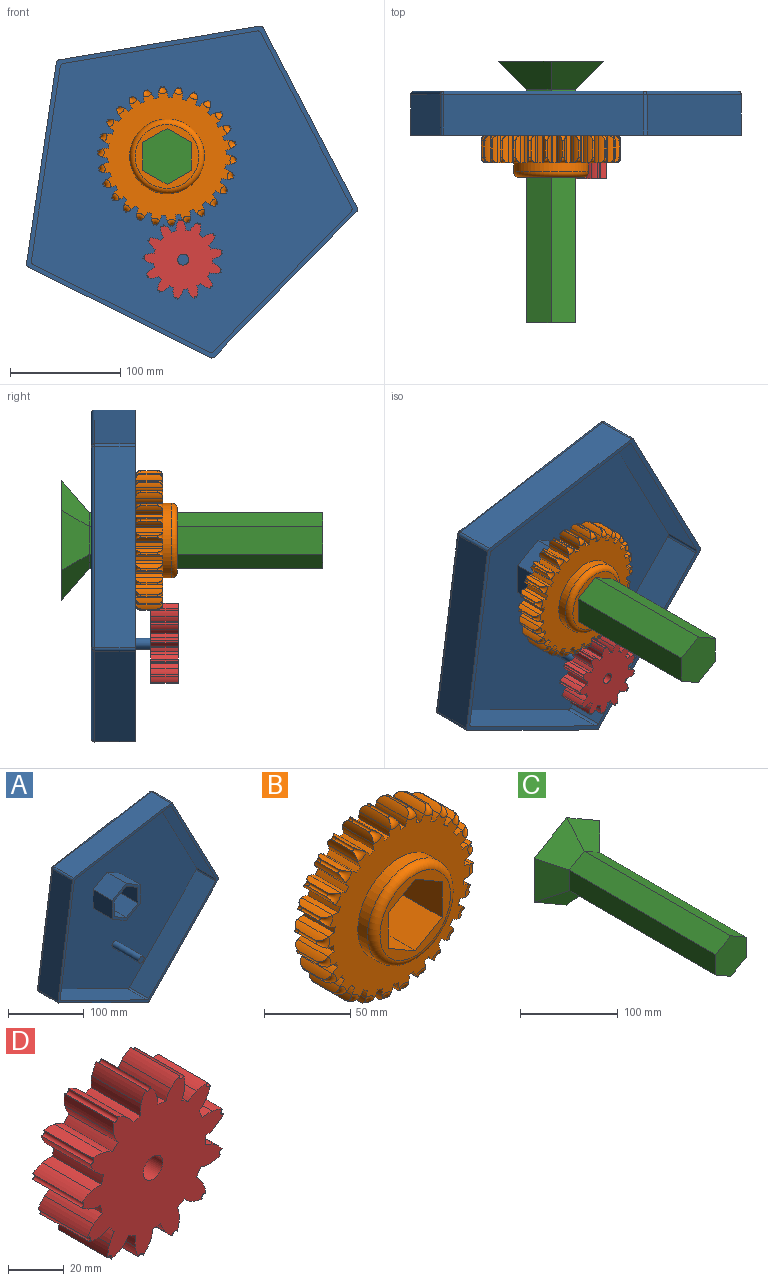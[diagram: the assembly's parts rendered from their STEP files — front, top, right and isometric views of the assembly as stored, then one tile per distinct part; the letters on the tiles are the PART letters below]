
ASSEMBLY  parts=4 mates=3
PART A: 48 faces, bbox 300.4x54x301.4 mm
  f0: plane 301.37x300.44mm, normal (0,-1,0), area 3719.9mm2, adj f6,f7,f8,f9,f10,f19,f20,f21
  f1: plane 40x22mm, normal (-0.5,0,-0.87), area 1016mm2, adj f2,f11,f12,f13
  f2: plane 40x25.4mm, normal (-1,0,0), area 1016mm2, adj f1,f3,f12,f13
  f3: plane 40x22mm, normal (-0.5,0,0.87), area 1016mm2, adj f2,f4,f12,f13
  f4: plane 40x22mm, normal (0.5,0,0.87), area 1016mm2, adj f3,f5,f12,f13
  f5: plane 40x25.4mm, normal (1,0,0), area 1016mm2, adj f4,f11,f12,f13
  f6: plane 131.78x129.19mm, normal (0.71,0,-0.7), area 6828mm2, adj f0,f39,f43,f45
  f7: plane 163.59x85.41mm, normal (0.89,0,0.46), area 6828mm2, adj f0,f36,f42,f45
  f8: plane 181.97x37mm, normal (-0.17,0,0.99), area 6828mm2, adj f0,f31,f36,f37
  f9: plane 182.55x37mm, normal (-0.99,0,0.15), area 6828mm2, adj f0,f31,f32,f33
  f10: plane 165.25x82.14mm, normal (-0.45,0,-0.9), area 6828mm2, adj f0,f33,f38,f39
  f11: plane 40x22mm, normal (0.5,0,-0.87), area 1016mm2, adj f1,f5,f12,f13
  f12: plane 60.04x51.99mm, normal (0,-1,0), area 665mm2, adj f1,f2,f3,f4,f5,f11,f14,f15
  f13: plane 295.37x294.44mm, normal (0,1,0), area 56915.8mm2, adj f1,f2,f3,f4,f5,f11,f32,f37
  f14: plane 36x26mm, normal (0.5,0,0.87), area 1080.7mm2, adj f12,f15,f24,f25
  f15: plane 36x30.02mm, normal (1,0,0), area 1080.7mm2, adj f12,f14,f16,f25
  f16: plane 36x26mm, normal (0.5,0,-0.87), area 1080.7mm2, adj f12,f15,f17,f25
  f17: plane 36x26mm, normal (-0.5,0,-0.87), area 1080.7mm2, adj f12,f16,f18,f25
  f18: plane 36x30.02mm, normal (-1,0,0), area 1080.7mm2, adj f12,f17,f24,f25
  f19: plane 127.63x125.12mm, normal (-0.71,0,0.7), area 6434.3mm2, adj f0,f25,f26,f30
  f20: plane 158.43x82.72mm, normal (-0.89,0,-0.46), area 6434.3mm2, adj f0,f25,f26,f27
  f21: plane 176.24x36mm, normal (0.17,0,-0.99), area 6434.3mm2, adj f0,f25,f27,f28
  f22: plane 176.8x36mm, normal (0.99,0,-0.15), area 6434.3mm2, adj f0,f25,f28,f29
  f23: plane 160.05x79.55mm, normal (0.45,0,0.9), area 6434.3mm2, adj f0,f25,f29,f30
  f24: plane 36x26mm, normal (-0.5,0,0.87), area 1080.7mm2, adj f12,f14,f18,f25
  f25: plane 292.07x291.17mm, normal (0,-1,0), area 55248.8mm2, adj f14,f15,f16,f17,f18,f19,f20,f21
  f26: cylinder r=3mm len=36mm, axis (0,-1,0), area 135.7mm2, adj f0,f19,f20,f25
  f27: cylinder r=3mm len=36mm, axis (0,-1,0), area 135.7mm2, adj f0,f20,f21,f25
  f28: cylinder r=3mm len=36mm, axis (0,-1,0), area 135.7mm2, adj f0,f21,f22,f25
  f29: cylinder r=3mm len=36mm, axis (0,-1,0), area 135.7mm2, adj f0,f22,f23,f25
  f30: cylinder r=3mm len=36mm, axis (0,-1,0), area 135.7mm2, adj f0,f19,f23,f25
  f31: cylinder r=3mm len=37mm, axis (0,1,0), area 139.5mm2, adj f0,f8,f9,f34
  f32: cylinder r=3mm len=182.99mm, axis (-0.15,0,-0.99), area 869.6mm2, adj f9,f13,f34,f35
  f33: cylinder r=3mm len=37mm, axis (0,1,0), area 139.5mm2, adj f0,f9,f10,f35
  f34: sphere r=3mm, area 11.3mm2, adj f31,f32,f37
  f35: sphere r=3mm, area 11.3mm2, adj f32,f33,f38
  f36: cylinder r=3mm len=37mm, axis (0,1,0), area 139.5mm2, adj f0,f7,f8,f40
  f37: cylinder r=3mm len=182.47mm, axis (-0.99,0,-0.17), area 869.6mm2, adj f8,f13,f34,f40
  f38: cylinder r=3mm len=166.59mm, axis (0.9,0,-0.45), area 869.6mm2, adj f10,f13,f35,f41
  f39: cylinder r=3mm len=37mm, axis (0,1,0), area 139.5mm2, adj f0,f6,f10,f41
  f40: sphere r=3mm, area 11.3mm2, adj f36,f37,f42
  f41: sphere r=3mm, area 11.3mm2, adj f38,f39,f43
  f42: cylinder r=3mm len=164.97mm, axis (-0.46,0,0.89), area 869.6mm2, adj f7,f13,f40,f44
  f43: cylinder r=3mm len=133.88mm, axis (0.7,0,0.71), area 869.6mm2, adj f6,f13,f41,f44
  f44: sphere r=3mm, area 11.3mm2, adj f42,f43,f45
  f45: cylinder r=3mm len=37mm, axis (0,1,0), area 139.5mm2, adj f0,f6,f7,f44
  f46: cylinder r=5mm len=50mm, axis (0,1,0), area 1570.8mm2, adj f25,f47
  f47: plane 10x10mm, normal (0,-1,0), area 78.5mm2, adj f46
PART B: 218 faces, bbox 128.7x38.1x128.8 mm
  f0: cylinder r=53.72mm len=25mm, axis (0,1,0), area 100.1mm2, adj f30,f31,f32,f133
  f1: cylinder r=53.72mm len=25mm, axis (0,1,0), area 100.1mm2, adj f31,f32,f126,f132
  f2: cylinder r=53.72mm len=25mm, axis (0,1,0), area 100.1mm2, adj f31,f32,f119,f125
  f3: cylinder r=53.72mm len=25mm, axis (0,1,0), area 100.1mm2, adj f31,f32,f112,f118
  f4: cylinder r=53.72mm len=25mm, axis (0,1,0), area 100.1mm2, adj f31,f32,f105,f111
  f5: cylinder r=53.72mm len=25mm, axis (0,1,0), area 100.1mm2, adj f31,f32,f98,f104
  f6: cylinder r=53.72mm len=25mm, axis (0,1,0), area 100.1mm2, adj f31,f32,f91,f97
  f7: cylinder r=53.72mm len=25mm, axis (0,1,0), area 100.1mm2, adj f31,f32,f84,f90
  f8: cylinder r=53.72mm len=25mm, axis (0,1,0), area 100.1mm2, adj f31,f32,f77,f83
  f9: cylinder r=53.72mm len=25mm, axis (0,1,0), area 100.1mm2, adj f31,f32,f70,f76
  f10: cylinder r=53.72mm len=25mm, axis (0,1,0), area 100.1mm2, adj f31,f32,f63,f69
  f11: cylinder r=53.72mm len=25mm, axis (0,1,0), area 100.1mm2, adj f31,f32,f56,f62
  f12: cylinder r=53.72mm len=25mm, axis (0,1,0), area 100.1mm2, adj f31,f32,f49,f55
  f13: cylinder r=53.72mm len=25mm, axis (0,1,0), area 100.1mm2, adj f31,f32,f48,f210
  f14: cylinder r=53.72mm len=25mm, axis (0,1,0), area 100.1mm2, adj f31,f32,f209,f214
  f15: cylinder r=53.72mm len=25mm, axis (0,1,0), area 100.1mm2, adj f31,f32,f202,f208
  f16: cylinder r=53.72mm len=25mm, axis (0,1,0), area 100.1mm2, adj f31,f32,f195,f201
  f17: cylinder r=53.72mm len=25mm, axis (0,1,0), area 100.1mm2, adj f31,f32,f188,f194
  f18: cylinder r=53.72mm len=25mm, axis (0,1,0), area 100.1mm2, adj f31,f32,f182,f187
  f19: cylinder r=53.72mm len=25mm, axis (0,1,0), area 100.1mm2, adj f31,f32,f175,f181
  f20: cylinder r=53.72mm len=25mm, axis (0,1,0), area 100.1mm2, adj f31,f32,f168,f174
  f21: cylinder r=53.72mm len=25mm, axis (0,1,0), area 100.1mm2, adj f31,f32,f161,f167
  f22: cylinder r=53.72mm len=25mm, axis (0,1,0), area 100.1mm2, adj f31,f32,f154,f160
  f23: cylinder r=53.72mm len=25mm, axis (0,1,0), area 100.1mm2, adj f31,f32,f147,f153
  f24: cylinder r=53.72mm len=25mm, axis (0,1,0), area 100.1mm2, adj f31,f32,f139,f146
  f25: cylinder r=53.72mm len=25mm, axis (0,1,0), area 100.1mm2, adj f26,f31,f32,f140
  f26: cylinder r=14.2mm len=25mm, axis (0,1,0), area 127.1mm2, adj f25,f27,f31,f32
  f27: cylinder r=14.99mm len=25mm, axis (0,1,0), area 128mm2, adj f26,f28,f31,f32,f33,f34
  f28: cylinder r=1.17mm len=14.84mm, axis (0,1,0), area 54.3mm2, adj f27,f29,f33,f34
  f29: cylinder r=14.99mm len=25mm, axis (0,1,0), area 128mm2, adj f28,f30,f31,f32,f33,f34
  f30: cylinder r=14.2mm len=25mm, axis (0,1,0), area 127.1mm2, adj f0,f29,f31,f32
  f31: plane 117.37x117.36mm, normal (0,-1,0), area 6357.2mm2, adj f0,f1,f2,f3,f4,f5,f6,f7
  f32: plane 119.73x117.37mm, normal (0,1,0), area 8340.6mm2, adj f0,f1,f2,f3,f4,f5,f6,f7
  f33: torus R=6.25mm, axis (0,-1,0), area 43.9mm2, adj f27,f28,f29,f32
  f34: torus R=6.25mm, axis (0,-1,0), area 43.9mm2, adj f27,f28,f29,f31
  f35: plane 38.1x25.4mm, normal (-1,0,0), area 967.7mm2, adj f32,f36,f40,f42
  f36: plane 38.1x22mm, normal (-0.5,0,0.87), area 967.7mm2, adj f32,f35,f37,f40
  f37: plane 38.1x22mm, normal (0.5,0,0.87), area 967.7mm2, adj f32,f36,f38,f40
  f38: plane 38.1x25.4mm, normal (1,0,0), area 967.7mm2, adj f32,f37,f39,f40
  f39: plane 38.1x22mm, normal (0.5,0,-0.87), area 967.7mm2, adj f32,f38,f40,f42
  f40: plane 57.81x57.81mm, normal (0,-1,0), area 948.4mm2, adj f35,f36,f37,f38,f39,f42,f217
  f41: cylinder r=33.98mm len=67.97mm, axis (0,1,0), area 1712.5mm2, adj f31,f217
  f42: plane 38.1x22mm, normal (-0.5,0,-0.87), area 967.7mm2, adj f32,f35,f39,f40
  f43: cylinder r=1.17mm len=14.84mm, axis (0,1,0), area 54.3mm2, adj f44,f45,f46,f47
  f44: torus R=6.25mm, axis (0,-1,0), area 43.9mm2, adj f31,f43,f45,f47
  f45: cylinder r=14.99mm len=25mm, axis (0,1,0), area 128mm2, adj f31,f32,f43,f44,f46,f49
  f46: torus R=6.25mm, axis (0,-1,0), area 43.9mm2, adj f32,f43,f45,f47
  f47: cylinder r=14.99mm len=25mm, axis (0,1,0), area 128mm2, adj f31,f32,f43,f44,f46,f48
  f48: cylinder r=14.2mm len=25mm, axis (0,1,0), area 127.1mm2, adj f13,f31,f32,f47
  f49: cylinder r=14.2mm len=25mm, axis (0,1,0), area 127.1mm2, adj f12,f31,f32,f45
  f50: cylinder r=1.17mm len=14.84mm, axis (0,1,0), area 54.3mm2, adj f51,f52,f53,f54
  f51: torus R=6.25mm, axis (0,-1,0), area 43.9mm2, adj f31,f50,f52,f54
  f52: cylinder r=14.99mm len=25mm, axis (0,1,0), area 128mm2, adj f31,f32,f50,f51,f53,f56
  f53: torus R=6.25mm, axis (0,-1,0), area 43.9mm2, adj f32,f50,f52,f54
  f54: cylinder r=14.99mm len=25mm, axis (0,1,0), area 128mm2, adj f31,f32,f50,f51,f53,f55
  f55: cylinder r=14.2mm len=25mm, axis (0,1,0), area 127.1mm2, adj f12,f31,f32,f54
  f56: cylinder r=14.2mm len=25mm, axis (0,1,0), area 127.1mm2, adj f11,f31,f32,f52
  f57: cylinder r=1.17mm len=14.84mm, axis (0,1,0), area 54.3mm2, adj f58,f59,f60,f61
  f58: torus R=6.25mm, axis (0,-1,0), area 43.9mm2, adj f31,f57,f59,f61
  f59: cylinder r=14.99mm len=25mm, axis (0,1,0), area 128mm2, adj f31,f32,f57,f58,f60,f63
  f60: torus R=6.25mm, axis (0,-1,0), area 43.9mm2, adj f32,f57,f59,f61
  f61: cylinder r=14.99mm len=25mm, axis (0,1,0), area 128mm2, adj f31,f32,f57,f58,f60,f62
  f62: cylinder r=14.2mm len=25mm, axis (0,1,0), area 127.1mm2, adj f11,f31,f32,f61
  f63: cylinder r=14.2mm len=25mm, axis (0,1,0), area 127.1mm2, adj f10,f31,f32,f59
  f64: cylinder r=1.17mm len=14.84mm, axis (0,1,0), area 54.3mm2, adj f65,f66,f67,f68
  f65: torus R=6.25mm, axis (0,-1,0), area 43.9mm2, adj f31,f64,f66,f68
  f66: cylinder r=14.99mm len=25mm, axis (0,1,0), area 128mm2, adj f31,f32,f64,f65,f67,f70
  f67: torus R=6.25mm, axis (0,-1,0), area 43.9mm2, adj f32,f64,f66,f68
  f68: cylinder r=14.99mm len=25mm, axis (0,1,0), area 128mm2, adj f31,f32,f64,f65,f67,f69
  f69: cylinder r=14.2mm len=25mm, axis (0,1,0), area 127.1mm2, adj f10,f31,f32,f68
  f70: cylinder r=14.2mm len=25mm, axis (0,1,0), area 127.1mm2, adj f9,f31,f32,f66
  f71: cylinder r=1.17mm len=14.84mm, axis (0,1,0), area 54.3mm2, adj f72,f73,f74,f75
  f72: torus R=6.25mm, axis (0,-1,0), area 43.9mm2, adj f31,f71,f73,f75
  f73: cylinder r=14.99mm len=25mm, axis (0,1,0), area 128mm2, adj f31,f32,f71,f72,f74,f77
  f74: torus R=6.25mm, axis (0,-1,0), area 43.9mm2, adj f32,f71,f73,f75
  f75: cylinder r=14.99mm len=25mm, axis (0,1,0), area 128mm2, adj f31,f32,f71,f72,f74,f76
  f76: cylinder r=14.2mm len=25mm, axis (0,1,0), area 127.1mm2, adj f9,f31,f32,f75
  f77: cylinder r=14.2mm len=25mm, axis (0,1,0), area 127.1mm2, adj f8,f31,f32,f73
  f78: cylinder r=1.17mm len=14.84mm, axis (0,1,0), area 54.3mm2, adj f79,f80,f81,f82
  f79: torus R=6.25mm, axis (0,-1,0), area 43.9mm2, adj f31,f78,f80,f82
  f80: cylinder r=14.99mm len=25mm, axis (0,1,0), area 128mm2, adj f31,f32,f78,f79,f81,f84
  f81: torus R=6.25mm, axis (0,-1,0), area 43.9mm2, adj f32,f78,f80,f82
  f82: cylinder r=14.99mm len=25mm, axis (0,1,0), area 128mm2, adj f31,f32,f78,f79,f81,f83
  f83: cylinder r=14.2mm len=25mm, axis (0,1,0), area 127.1mm2, adj f8,f31,f32,f82
  f84: cylinder r=14.2mm len=25mm, axis (0,1,0), area 127.1mm2, adj f7,f31,f32,f80
  f85: cylinder r=1.17mm len=14.84mm, axis (0,1,0), area 54.3mm2, adj f86,f87,f88,f89
  f86: torus R=6.25mm, axis (0,-1,0), area 43.9mm2, adj f31,f85,f87,f89
  f87: cylinder r=14.99mm len=25mm, axis (0,1,0), area 128mm2, adj f31,f32,f85,f86,f88,f91
  f88: torus R=6.25mm, axis (0,-1,0), area 43.9mm2, adj f32,f85,f87,f89
  f89: cylinder r=14.99mm len=25mm, axis (0,1,0), area 128mm2, adj f31,f32,f85,f86,f88,f90
  f90: cylinder r=14.2mm len=25mm, axis (0,1,0), area 127.1mm2, adj f7,f31,f32,f89
  f91: cylinder r=14.2mm len=25mm, axis (0,1,0), area 127.1mm2, adj f6,f31,f32,f87
  f92: cylinder r=1.17mm len=14.84mm, axis (0,1,0), area 54.3mm2, adj f93,f94,f95,f96
  f93: torus R=6.25mm, axis (0,-1,0), area 43.9mm2, adj f31,f92,f94,f96
  f94: cylinder r=14.99mm len=25mm, axis (0,1,0), area 128mm2, adj f31,f32,f92,f93,f95,f98
  f95: torus R=6.25mm, axis (0,-1,0), area 43.9mm2, adj f32,f92,f94,f96
  f96: cylinder r=14.99mm len=25mm, axis (0,1,0), area 128mm2, adj f31,f32,f92,f93,f95,f97
  f97: cylinder r=14.2mm len=25mm, axis (0,1,0), area 127.1mm2, adj f6,f31,f32,f96
  f98: cylinder r=14.2mm len=25mm, axis (0,1,0), area 127.1mm2, adj f5,f31,f32,f94
  f99: cylinder r=1.17mm len=14.84mm, axis (0,1,0), area 54.3mm2, adj f100,f101,f102,f103
  f100: torus R=6.25mm, axis (0,-1,0), area 43.9mm2, adj f31,f99,f101,f103
  f101: cylinder r=14.99mm len=25mm, axis (0,1,0), area 128mm2, adj f31,f32,f99,f100,f102,f105
  f102: torus R=6.25mm, axis (0,-1,0), area 43.9mm2, adj f32,f99,f101,f103
  f103: cylinder r=14.99mm len=25mm, axis (0,1,0), area 128mm2, adj f31,f32,f99,f100,f102,f104
  f104: cylinder r=14.2mm len=25mm, axis (0,1,0), area 127.1mm2, adj f5,f31,f32,f103
  f105: cylinder r=14.2mm len=25mm, axis (0,1,0), area 127.1mm2, adj f4,f31,f32,f101
  f106: cylinder r=1.17mm len=14.84mm, axis (0,1,0), area 54.3mm2, adj f107,f108,f109,f110
  f107: torus R=6.25mm, axis (0,-1,0), area 43.9mm2, adj f31,f106,f108,f110
  f108: cylinder r=14.99mm len=25mm, axis (0,1,0), area 128mm2, adj f31,f32,f106,f107,f109,f112
  f109: torus R=6.25mm, axis (0,-1,0), area 43.9mm2, adj f32,f106,f108,f110
  f110: cylinder r=14.99mm len=25mm, axis (0,1,0), area 128mm2, adj f31,f32,f106,f107,f109,f111
  f111: cylinder r=14.2mm len=25mm, axis (0,1,0), area 127.1mm2, adj f4,f31,f32,f110
  f112: cylinder r=14.2mm len=25mm, axis (0,1,0), area 127.1mm2, adj f3,f31,f32,f108
  f113: cylinder r=1.17mm len=14.84mm, axis (0,1,0), area 54.3mm2, adj f114,f115,f116,f117
  f114: torus R=6.25mm, axis (0,-1,0), area 43.9mm2, adj f31,f113,f115,f117
  f115: cylinder r=14.99mm len=25mm, axis (0,1,0), area 128mm2, adj f31,f32,f113,f114,f116,f119
  f116: torus R=6.25mm, axis (0,-1,0), area 43.9mm2, adj f32,f113,f115,f117
  f117: cylinder r=14.99mm len=25mm, axis (0,1,0), area 128mm2, adj f31,f32,f113,f114,f116,f118
  f118: cylinder r=14.2mm len=25mm, axis (0,1,0), area 127.1mm2, adj f3,f31,f32,f117
  f119: cylinder r=14.2mm len=25mm, axis (0,1,0), area 127.1mm2, adj f2,f31,f32,f115
  f120: cylinder r=1.17mm len=14.84mm, axis (0,1,0), area 54.3mm2, adj f121,f122,f123,f124
  f121: torus R=6.25mm, axis (0,-1,0), area 43.9mm2, adj f31,f120,f122,f124
  f122: cylinder r=14.99mm len=25mm, axis (0,1,0), area 128mm2, adj f31,f32,f120,f121,f123,f126
  f123: torus R=6.25mm, axis (0,-1,0), area 43.9mm2, adj f32,f120,f122,f124
  f124: cylinder r=14.99mm len=25mm, axis (0,1,0), area 128mm2, adj f31,f32,f120,f121,f123,f125
  f125: cylinder r=14.2mm len=25mm, axis (0,1,0), area 127.1mm2, adj f2,f31,f32,f124
  f126: cylinder r=14.2mm len=25mm, axis (0,1,0), area 127.1mm2, adj f1,f31,f32,f122
  f127: cylinder r=1.17mm len=14.84mm, axis (0,1,0), area 54.3mm2, adj f128,f129,f130,f131
  f128: torus R=6.25mm, axis (0,-1,0), area 43.9mm2, adj f31,f127,f129,f131
  f129: cylinder r=14.99mm len=25mm, axis (0,1,0), area 128mm2, adj f31,f32,f127,f128,f130,f133
  f130: torus R=6.25mm, axis (0,-1,0), area 43.9mm2, adj f32,f127,f129,f131
  f131: cylinder r=14.99mm len=25mm, axis (0,1,0), area 128mm2, adj f31,f32,f127,f128,f130,f132
  f132: cylinder r=14.2mm len=25mm, axis (0,1,0), area 127.1mm2, adj f1,f31,f32,f131
  f133: cylinder r=14.2mm len=25mm, axis (0,1,0), area 127.1mm2, adj f0,f31,f32,f129
  f134: cylinder r=1.17mm len=14.84mm, axis (0,1,0), area 54.3mm2, adj f135,f136,f137,f138
  f135: torus R=6.25mm, axis (0,-1,0), area 43.9mm2, adj f31,f134,f136,f138
  f136: cylinder r=14.99mm len=25mm, axis (0,1,0), area 128mm2, adj f31,f32,f134,f135,f137,f139
  f137: torus R=6.25mm, axis (0,-1,0), area 43.9mm2, adj f32,f134,f136,f138
  f138: cylinder r=14.99mm len=25mm, axis (0,1,0), area 128mm2, adj f31,f32,f134,f135,f137,f140
  f139: cylinder r=14.2mm len=25mm, axis (0,1,0), area 127.1mm2, adj f24,f31,f32,f136
  f140: cylinder r=14.2mm len=25mm, axis (0,1,0), area 127.1mm2, adj f25,f31,f32,f138
  f141: cylinder r=1.17mm len=14.84mm, axis (0,1,0), area 54.3mm2, adj f142,f143,f144,f145
  f142: torus R=6.25mm, axis (0,-1,0), area 43.9mm2, adj f31,f141,f143,f145
  f143: cylinder r=14.99mm len=25mm, axis (0,1,0), area 128mm2, adj f31,f32,f141,f142,f144,f147
  f144: torus R=6.25mm, axis (0,-1,0), area 43.9mm2, adj f32,f141,f143,f145
  f145: cylinder r=14.99mm len=25mm, axis (0,1,0), area 128mm2, adj f31,f32,f141,f142,f144,f146
  f146: cylinder r=14.2mm len=25mm, axis (0,1,0), area 127.1mm2, adj f24,f31,f32,f145
  f147: cylinder r=14.2mm len=25mm, axis (0,1,0), area 127.1mm2, adj f23,f31,f32,f143
  f148: cylinder r=1.17mm len=14.84mm, axis (0,1,0), area 54.3mm2, adj f149,f150,f151,f152
  f149: torus R=6.25mm, axis (0,-1,0), area 43.9mm2, adj f31,f148,f150,f152
  f150: cylinder r=14.99mm len=25mm, axis (0,1,0), area 128mm2, adj f31,f32,f148,f149,f151,f154
  f151: torus R=6.25mm, axis (0,-1,0), area 43.9mm2, adj f32,f148,f150,f152
  f152: cylinder r=14.99mm len=25mm, axis (0,1,0), area 128mm2, adj f31,f32,f148,f149,f151,f153
  f153: cylinder r=14.2mm len=25mm, axis (0,1,0), area 127.1mm2, adj f23,f31,f32,f152
  f154: cylinder r=14.2mm len=25mm, axis (0,1,0), area 127.1mm2, adj f22,f31,f32,f150
  f155: cylinder r=1.17mm len=14.84mm, axis (0,1,0), area 54.3mm2, adj f156,f157,f158,f159
  f156: torus R=6.25mm, axis (0,-1,0), area 43.9mm2, adj f31,f155,f157,f159
  f157: cylinder r=14.99mm len=25mm, axis (0,1,0), area 128mm2, adj f31,f32,f155,f156,f158,f161
  f158: torus R=6.25mm, axis (0,-1,0), area 43.9mm2, adj f32,f155,f157,f159
  f159: cylinder r=14.99mm len=25mm, axis (0,1,0), area 128mm2, adj f31,f32,f155,f156,f158,f160
  f160: cylinder r=14.2mm len=25mm, axis (0,1,0), area 127.1mm2, adj f22,f31,f32,f159
  f161: cylinder r=14.2mm len=25mm, axis (0,1,0), area 127.1mm2, adj f21,f31,f32,f157
  f162: cylinder r=1.17mm len=14.84mm, axis (0,1,0), area 54.3mm2, adj f163,f164,f165,f166
  f163: torus R=6.25mm, axis (0,-1,0), area 43.9mm2, adj f31,f162,f164,f166
  f164: cylinder r=14.99mm len=25mm, axis (0,1,0), area 128mm2, adj f31,f32,f162,f163,f165,f168
  f165: torus R=6.25mm, axis (0,-1,0), area 43.9mm2, adj f32,f162,f164,f166
  f166: cylinder r=14.99mm len=25mm, axis (0,1,0), area 128mm2, adj f31,f32,f162,f163,f165,f167
  f167: cylinder r=14.2mm len=25mm, axis (0,1,0), area 127.1mm2, adj f21,f31,f32,f166
  f168: cylinder r=14.2mm len=25mm, axis (0,1,0), area 127.1mm2, adj f20,f31,f32,f164
  f169: cylinder r=1.17mm len=14.84mm, axis (0,1,0), area 54.3mm2, adj f170,f171,f172,f173
  f170: torus R=6.25mm, axis (0,-1,0), area 43.9mm2, adj f31,f169,f171,f173
  f171: cylinder r=14.99mm len=25mm, axis (0,1,0), area 128mm2, adj f31,f32,f169,f170,f172,f175
  f172: torus R=6.25mm, axis (0,-1,0), area 43.9mm2, adj f32,f169,f171,f173
  f173: cylinder r=14.99mm len=25mm, axis (0,1,0), area 128mm2, adj f31,f32,f169,f170,f172,f174
  f174: cylinder r=14.2mm len=25mm, axis (0,1,0), area 127.1mm2, adj f20,f31,f32,f173
  f175: cylinder r=14.2mm len=25mm, axis (0,1,0), area 127.1mm2, adj f19,f31,f32,f171
  f176: cylinder r=1.17mm len=14.84mm, axis (0,1,0), area 54.3mm2, adj f177,f178,f179,f180
  f177: torus R=6.25mm, axis (0,-1,0), area 43.9mm2, adj f31,f176,f178,f180
  f178: cylinder r=14.99mm len=25mm, axis (0,1,0), area 128mm2, adj f31,f32,f176,f177,f179,f182
  f179: torus R=6.25mm, axis (0,-1,0), area 43.9mm2, adj f32,f176,f178,f180
  f180: cylinder r=14.99mm len=25mm, axis (0,1,0), area 128mm2, adj f31,f32,f176,f177,f179,f181
  f181: cylinder r=14.2mm len=25mm, axis (0,1,0), area 127.1mm2, adj f19,f31,f32,f180
  f182: cylinder r=14.2mm len=25mm, axis (0,1,0), area 127.1mm2, adj f18,f31,f32,f178
  f183: torus R=6.25mm, axis (0,-1,0), area 43.9mm2, adj f31,f184,f185,f186
  f184: cylinder r=14.99mm len=25mm, axis (0,1,0), area 134.6mm2, adj f31,f32,f183,f185,f188
  f185: cylinder r=1.17mm len=19.92mm, axis (0,1,0), area 72.9mm2, adj f32,f183,f184,f186
  f186: cylinder r=14.99mm len=25mm, axis (0,1,0), area 134.6mm2, adj f31,f32,f183,f185,f187
  f187: cylinder r=14.2mm len=25mm, axis (0,1,0), area 127.1mm2, adj f18,f31,f32,f186
  f188: cylinder r=14.2mm len=25mm, axis (0,1,0), area 127.1mm2, adj f17,f31,f32,f184
  f189: cylinder r=1.17mm len=14.84mm, axis (0,1,0), area 54.3mm2, adj f190,f191,f192,f193
  f190: torus R=6.25mm, axis (0,-1,0), area 43.9mm2, adj f31,f189,f191,f193
  f191: cylinder r=14.99mm len=25mm, axis (0,1,0), area 128mm2, adj f31,f32,f189,f190,f192,f195
  f192: torus R=6.25mm, axis (0,-1,0), area 43.9mm2, adj f32,f189,f191,f193
  f193: cylinder r=14.99mm len=25mm, axis (0,1,0), area 128mm2, adj f31,f32,f189,f190,f192,f194
  f194: cylinder r=14.2mm len=25mm, axis (0,1,0), area 127.1mm2, adj f17,f31,f32,f193
  f195: cylinder r=14.2mm len=25mm, axis (0,1,0), area 127.1mm2, adj f16,f31,f32,f191
  f196: cylinder r=1.17mm len=14.84mm, axis (0,1,0), area 54.3mm2, adj f197,f198,f199,f200
  f197: torus R=6.25mm, axis (0,-1,0), area 43.9mm2, adj f31,f196,f198,f200
  f198: cylinder r=14.99mm len=25mm, axis (0,1,0), area 128mm2, adj f31,f32,f196,f197,f199,f202
  f199: torus R=6.25mm, axis (0,-1,0), area 43.9mm2, adj f32,f196,f198,f200
  f200: cylinder r=14.99mm len=25mm, axis (0,1,0), area 128mm2, adj f31,f32,f196,f197,f199,f201
  f201: cylinder r=14.2mm len=25mm, axis (0,1,0), area 127.1mm2, adj f16,f31,f32,f200
  f202: cylinder r=14.2mm len=25mm, axis (0,1,0), area 127.1mm2, adj f15,f31,f32,f198
  f203: cylinder r=1.17mm len=14.84mm, axis (0,1,0), area 54.3mm2, adj f204,f205,f206,f207
  f204: torus R=6.25mm, axis (0,-1,0), area 43.9mm2, adj f31,f203,f205,f207
  f205: cylinder r=14.99mm len=25mm, axis (0,1,0), area 128mm2, adj f31,f32,f203,f204,f206,f209
  f206: torus R=6.25mm, axis (0,-1,0), area 43.9mm2, adj f32,f203,f205,f207
  f207: cylinder r=14.99mm len=25mm, axis (0,1,0), area 128mm2, adj f31,f32,f203,f204,f206,f208
  f208: cylinder r=14.2mm len=25mm, axis (0,1,0), area 127.1mm2, adj f15,f31,f32,f207
  f209: cylinder r=14.2mm len=25mm, axis (0,1,0), area 127.1mm2, adj f14,f31,f32,f205
  f210: cylinder r=14.2mm len=25mm, axis (0,1,0), area 127.1mm2, adj f13,f31,f32,f211
  f211: cylinder r=14.99mm len=25mm, axis (0,1,0), area 128mm2, adj f31,f32,f210,f212,f215,f216
  f212: cylinder r=1.17mm len=14.84mm, axis (0,1,0), area 54.3mm2, adj f211,f213,f215,f216
  f213: cylinder r=14.99mm len=25mm, axis (0,1,0), area 128mm2, adj f31,f32,f212,f214,f215,f216
  f214: cylinder r=14.2mm len=25mm, axis (0,1,0), area 127.1mm2, adj f14,f31,f32,f213
  f215: torus R=6.25mm, axis (0,-1,0), area 43.9mm2, adj f32,f211,f212,f213
  f216: torus R=6.25mm, axis (0,-1,0), area 43.9mm2, adj f31,f211,f212,f213
  f217: torus R=28.9mm, axis (0,-1,0), area 1611.3mm2, adj f40,f41
PART C: 14 faces, bbox 94.8x237.2x109.5 mm
  f0: plane 211.84x25.4mm, normal (1,0,0), area 5380.6mm2, adj f1,f5,f6,f7
  f1: plane 211.84x22mm, normal (0.5,0,0.87), area 5380.6mm2, adj f0,f2,f6,f12
  f2: plane 211.84x22mm, normal (-0.5,0,0.87), area 5380.6mm2, adj f1,f3,f6,f11
  f3: plane 211.84x25.4mm, normal (-1,0,0), area 5380.6mm2, adj f2,f4,f6,f10
  f4: plane 211.84x22mm, normal (-0.5,0,-0.87), area 5380.6mm2, adj f3,f5,f6,f9
  f5: plane 211.84x22mm, normal (0.5,0,-0.87), area 5380.6mm2, adj f0,f4,f6,f8
  f6: plane 50.8x43.99mm, normal (0,-1,0), area 1676.2mm2, adj f0,f1,f2,f3,f4,f5
  f7: plane 54.73x25.4mm, normal (0.71,-0.71,0), area 1439.2mm2, adj f0,f8,f12,f13
  f8: plane 47.4x42.03mm, normal (0.35,-0.71,-0.61), area 1439.2mm2, adj f5,f7,f9,f13
  f9: plane 47.4x42.03mm, normal (-0.35,-0.71,-0.61), area 1439.2mm2, adj f4,f8,f10,f13
  f10: plane 54.73x25.4mm, normal (-0.71,-0.71,0), area 1439.2mm2, adj f3,f9,f11,f13
  f11: plane 47.4x42.03mm, normal (-0.35,-0.71,0.61), area 1439.2mm2, adj f2,f10,f12,f13
  f12: plane 47.4x42.03mm, normal (0.35,-0.71,0.61), area 1439.2mm2, adj f1,f7,f11,f13
  f13: plane 109.46x94.79mm, normal (0,1,0), area 7782mm2, adj f7,f8,f9,f10,f11,f12
PART D: 81 faces, bbox 72.4x25x72.5 mm
  f0: cylinder r=26.86mm len=25mm, axis (0,1,0), area 99.2mm2, adj f17,f19,f20,f50
  f1: cylinder r=26.86mm len=25mm, axis (0,1,0), area 99.2mm2, adj f19,f20,f45,f49
  f2: cylinder r=26.86mm len=25mm, axis (0,1,0), area 99.2mm2, adj f19,f20,f40,f44
  f3: cylinder r=26.86mm len=25mm, axis (0,1,0), area 99.2mm2, adj f19,f20,f35,f39
  f4: cylinder r=26.86mm len=25mm, axis (0,1,0), area 99.2mm2, adj f19,f20,f30,f34
  f5: cylinder r=26.86mm len=25mm, axis (0,1,0), area 99.2mm2, adj f19,f20,f25,f29
  f6: cylinder r=26.86mm len=25mm, axis (0,1,0), area 99.2mm2, adj f19,f20,f24,f76
  f7: cylinder r=26.86mm len=25mm, axis (0,1,0), area 99.2mm2, adj f19,f20,f75,f80
  f8: cylinder r=26.86mm len=25mm, axis (0,1,0), area 99.2mm2, adj f19,f20,f70,f74
  f9: cylinder r=26.86mm len=25mm, axis (0,1,0), area 99.2mm2, adj f19,f20,f65,f69
  f10: cylinder r=26.86mm len=25mm, axis (0,1,0), area 99.2mm2, adj f19,f20,f60,f64
  f11: cylinder r=26.86mm len=25mm, axis (0,1,0), area 99.2mm2, adj f19,f20,f54,f59
  f12: cylinder r=26.86mm len=25mm, axis (0,1,0), area 99.2mm2, adj f13,f19,f20,f55
  f13: cylinder r=14.2mm len=25mm, axis (0,1,0), area 125.1mm2, adj f12,f14,f19,f20
  f14: cylinder r=14.99mm len=25mm, axis (0,1,0), area 141.3mm2, adj f13,f15,f19,f20
  f15: cylinder r=1.17mm len=25mm, axis (0,1,0), area 91.6mm2, adj f14,f16,f19,f20
  f16: cylinder r=14.99mm len=25mm, axis (0,1,0), area 141.3mm2, adj f15,f17,f19,f20
  f17: cylinder r=14.2mm len=25mm, axis (0,1,0), area 127.1mm2, adj f0,f16,f19,f20
  f18: cylinder r=5mm len=25mm, axis (0,1,0), area 785.4mm2, adj f19,f20
  f19: plane 72.46x72.36mm, normal (0,-1,0), area 3036mm2, adj f0,f1,f2,f3,f4,f5,f6,f7
  f20: plane 72.46x72.36mm, normal (0,1,0), area 3036mm2, adj f0,f1,f2,f3,f4,f5,f6,f7
  f21: cylinder r=14.99mm len=25mm, axis (0,1,0), area 141.3mm2, adj f19,f20,f22,f25
  f22: cylinder r=1.17mm len=25mm, axis (0,1,0), area 91.6mm2, adj f19,f20,f21,f23
  f23: cylinder r=14.99mm len=25mm, axis (0,1,0), area 141.3mm2, adj f19,f20,f22,f24
  f24: cylinder r=14.2mm len=25mm, axis (0,1,0), area 127.1mm2, adj f6,f19,f20,f23
  f25: cylinder r=14.2mm len=25mm, axis (0,1,0), area 125.1mm2, adj f5,f19,f20,f21
  f26: cylinder r=14.99mm len=25mm, axis (0,1,0), area 141.3mm2, adj f19,f20,f27,f30
  f27: cylinder r=1.17mm len=25mm, axis (0,1,0), area 91.6mm2, adj f19,f20,f26,f28
  f28: cylinder r=14.99mm len=25mm, axis (0,1,0), area 141.3mm2, adj f19,f20,f27,f29
  f29: cylinder r=14.2mm len=25mm, axis (0,1,0), area 127.1mm2, adj f5,f19,f20,f28
  f30: cylinder r=14.2mm len=25mm, axis (0,1,0), area 125.1mm2, adj f4,f19,f20,f26
  f31: cylinder r=14.99mm len=25mm, axis (0,1,0), area 141.3mm2, adj f19,f20,f32,f35
  f32: cylinder r=1.17mm len=25mm, axis (0,1,0), area 91.6mm2, adj f19,f20,f31,f33
  f33: cylinder r=14.99mm len=25mm, axis (0,1,0), area 141.3mm2, adj f19,f20,f32,f34
  f34: cylinder r=14.2mm len=25mm, axis (0,1,0), area 127.1mm2, adj f4,f19,f20,f33
  f35: cylinder r=14.2mm len=25mm, axis (0,1,0), area 125.1mm2, adj f3,f19,f20,f31
  f36: cylinder r=14.99mm len=25mm, axis (0,1,0), area 141.3mm2, adj f19,f20,f37,f40
  f37: cylinder r=1.17mm len=25mm, axis (0,1,0), area 91.6mm2, adj f19,f20,f36,f38
  f38: cylinder r=14.99mm len=25mm, axis (0,1,0), area 141.3mm2, adj f19,f20,f37,f39
  f39: cylinder r=14.2mm len=25mm, axis (0,1,0), area 127.1mm2, adj f3,f19,f20,f38
  f40: cylinder r=14.2mm len=25mm, axis (0,1,0), area 125.1mm2, adj f2,f19,f20,f36
  f41: cylinder r=14.99mm len=25mm, axis (0,1,0), area 141.3mm2, adj f19,f20,f42,f45
  f42: cylinder r=1.17mm len=25mm, axis (0,1,0), area 91.6mm2, adj f19,f20,f41,f43
  f43: cylinder r=14.99mm len=25mm, axis (0,1,0), area 141.3mm2, adj f19,f20,f42,f44
  f44: cylinder r=14.2mm len=25mm, axis (0,1,0), area 127.1mm2, adj f2,f19,f20,f43
  f45: cylinder r=14.2mm len=25mm, axis (0,1,0), area 125.1mm2, adj f1,f19,f20,f41
  f46: cylinder r=14.99mm len=25mm, axis (0,1,0), area 141.3mm2, adj f19,f20,f47,f50
  f47: cylinder r=1.17mm len=25mm, axis (0,1,0), area 91.6mm2, adj f19,f20,f46,f48
  f48: cylinder r=14.99mm len=25mm, axis (0,1,0), area 141.3mm2, adj f19,f20,f47,f49
  f49: cylinder r=14.2mm len=25mm, axis (0,1,0), area 127.1mm2, adj f1,f19,f20,f48
  f50: cylinder r=14.2mm len=25mm, axis (0,1,0), area 125.1mm2, adj f0,f19,f20,f46
  f51: cylinder r=14.99mm len=25mm, axis (0,1,0), area 141.3mm2, adj f19,f20,f52,f54
  f52: cylinder r=1.17mm len=25mm, axis (0,1,0), area 91.6mm2, adj f19,f20,f51,f53
  f53: cylinder r=14.99mm len=25mm, axis (0,1,0), area 141.3mm2, adj f19,f20,f52,f55
  f54: cylinder r=14.2mm len=25mm, axis (0,1,0), area 125.1mm2, adj f11,f19,f20,f51
  f55: cylinder r=14.2mm len=25mm, axis (0,1,0), area 127.1mm2, adj f12,f19,f20,f53
  f56: cylinder r=14.99mm len=25mm, axis (0,1,0), area 141.3mm2, adj f19,f20,f57,f60
  f57: cylinder r=1.17mm len=25mm, axis (0,1,0), area 91.6mm2, adj f19,f20,f56,f58
  f58: cylinder r=14.99mm len=25mm, axis (0,1,0), area 141.3mm2, adj f19,f20,f57,f59
  f59: cylinder r=14.2mm len=25mm, axis (0,1,0), area 127.1mm2, adj f11,f19,f20,f58
  f60: cylinder r=14.2mm len=25mm, axis (0,1,0), area 125.1mm2, adj f10,f19,f20,f56
  f61: cylinder r=14.99mm len=25mm, axis (0,1,0), area 141.3mm2, adj f19,f20,f62,f65
  f62: cylinder r=1.17mm len=25mm, axis (0,1,0), area 91.6mm2, adj f19,f20,f61,f63
  f63: cylinder r=14.99mm len=25mm, axis (0,1,0), area 141.3mm2, adj f19,f20,f62,f64
  f64: cylinder r=14.2mm len=25mm, axis (0,1,0), area 127.1mm2, adj f10,f19,f20,f63
  f65: cylinder r=14.2mm len=25mm, axis (0,1,0), area 125.1mm2, adj f9,f19,f20,f61
  f66: cylinder r=14.99mm len=25mm, axis (0,1,0), area 141.3mm2, adj f19,f20,f67,f70
  f67: cylinder r=1.17mm len=25mm, axis (0,1,0), area 91.6mm2, adj f19,f20,f66,f68
  f68: cylinder r=14.99mm len=25mm, axis (0,1,0), area 141.3mm2, adj f19,f20,f67,f69
  f69: cylinder r=14.2mm len=25mm, axis (0,1,0), area 127.1mm2, adj f9,f19,f20,f68
  f70: cylinder r=14.2mm len=25mm, axis (0,1,0), area 125.1mm2, adj f8,f19,f20,f66
  f71: cylinder r=14.99mm len=25mm, axis (0,1,0), area 141.3mm2, adj f19,f20,f72,f75
  f72: cylinder r=1.17mm len=25mm, axis (0,1,0), area 91.6mm2, adj f19,f20,f71,f73
  f73: cylinder r=14.99mm len=25mm, axis (0,1,0), area 141.3mm2, adj f19,f20,f72,f74
  f74: cylinder r=14.2mm len=25mm, axis (0,1,0), area 127.1mm2, adj f8,f19,f20,f73
  f75: cylinder r=14.2mm len=25mm, axis (0,1,0), area 125.1mm2, adj f7,f19,f20,f71
  f76: cylinder r=14.2mm len=25mm, axis (0,1,0), area 125.1mm2, adj f6,f19,f20,f77
  f77: cylinder r=14.99mm len=25mm, axis (0,1,0), area 141.3mm2, adj f19,f20,f76,f78
  f78: cylinder r=1.17mm len=25mm, axis (0,1,0), area 91.6mm2, adj f19,f20,f77,f79
  f79: cylinder r=14.99mm len=25mm, axis (0,1,0), area 141.3mm2, adj f19,f20,f78,f80
  f80: cylinder r=14.2mm len=25mm, axis (0,1,0), area 127.1mm2, adj f7,f19,f20,f79
PLACE A t=(-250.77,-58.5,-14.99)mm fixed
PLACE B t=(-265.37,-98.5,10.21)mm
PLACE C t=(-262.59,-56.77,9.3)mm
PLACE D t=(-250.77,-112.5,-83.45)mm
MATE fastened A.f46 <-> D.f18  axis (0,-1,0) through (-250.77,-112.5,-83.45)mm
MATE slider C.f6 <-> B.f41  axis (0,-1,0) through (-265.37,-268.6,10.21)mm
MATE fastened A.f12 <-> B.f32  axis (0,-1,0) through (-265.16,-98.5,10.14)mm
